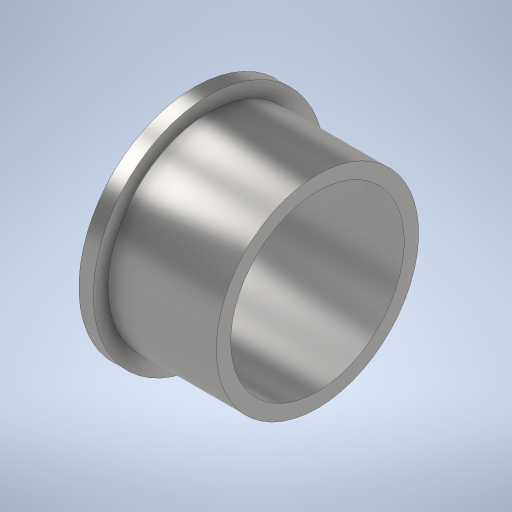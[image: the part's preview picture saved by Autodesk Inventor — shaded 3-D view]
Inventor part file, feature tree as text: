
AUTODESK INVENTOR PART (.ipt)
format: ipt  version: 2023.2 (Build 272271000, 271)  size: 281,088 bytes
history: native  units: mm
features: revolve x1, sketch x1
ambient origin geometry x8: Origin, YZ Plane, XZ Plane, XY Plane, X Axis, Y Axis, Z Axis, Center Point
bodies: Solid1 (feature_tree)
feature tree (2):
  revolve  "Revolution1"  [1 undecoded]
  sketch  "Sketch1"  dims[d0=8.0mm d1=1.0mm d2=1.0mm d3=7.5mm d4=1.0mm d5=90.0deg]
note: 1 required parameter value undecoded (feature->parameter linkage not recoverable at this tier; creation-order binding heuristic only, values carry confidence <= 0.55)
